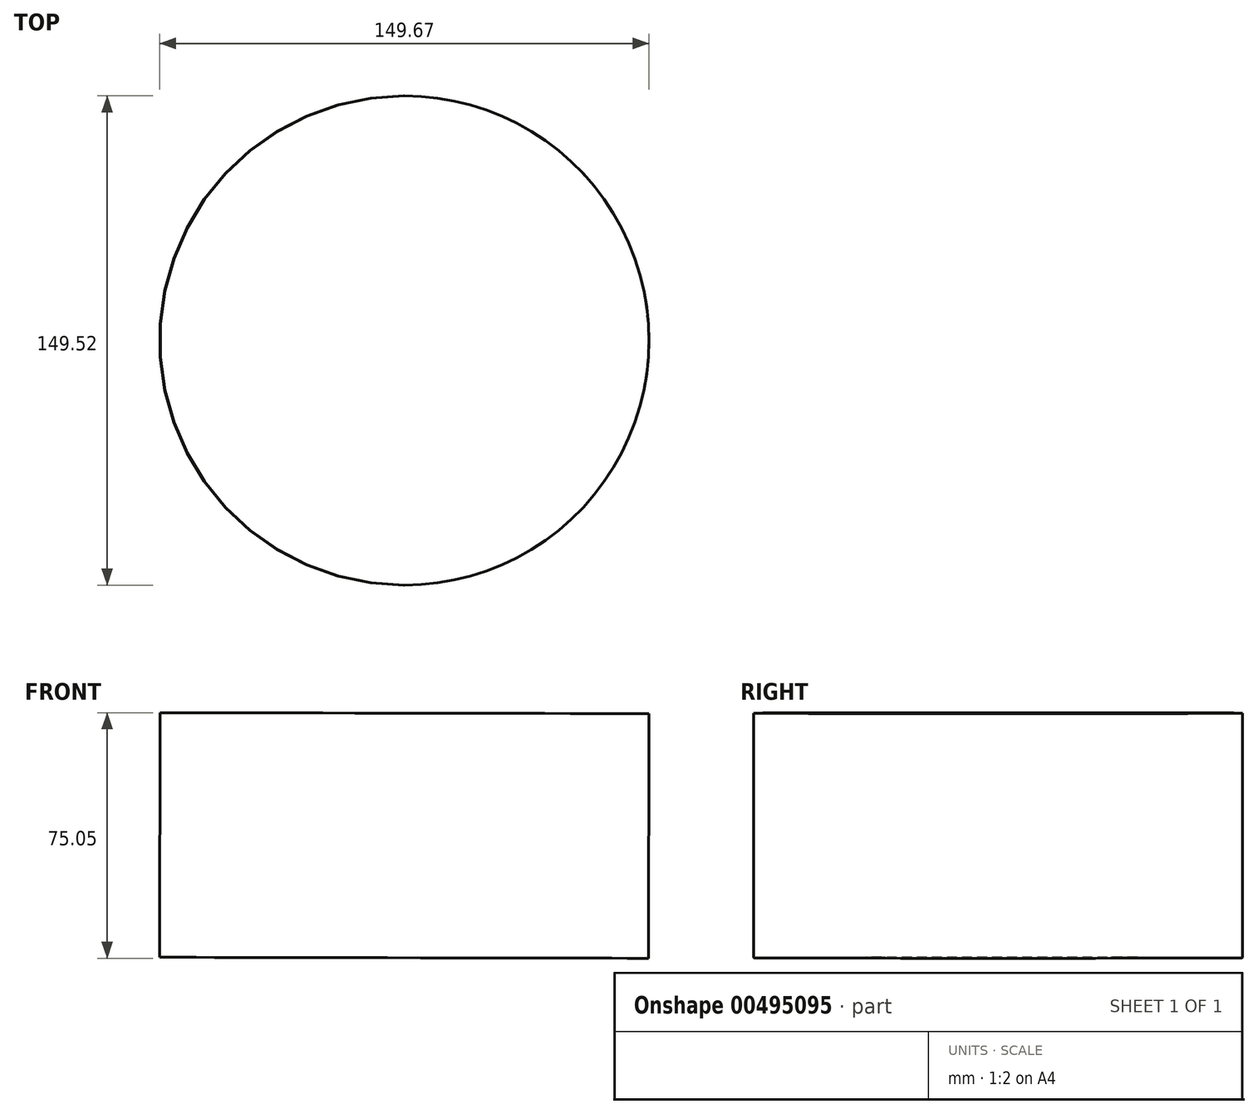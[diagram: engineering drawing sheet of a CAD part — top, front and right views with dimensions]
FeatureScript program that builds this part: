
annotation { "Feature Type Name" : "Feature", "Feature Type Description" : "" }
export const myFeature = defineFeature(function(context is Context, id is Id, definition is map)
    precondition{}
    {
        {
            var Q0;
            Q0=qCreatedBy(makeId("Front.planeOp"),FACE);
            var sketch = newSketch(context, id + "F0", { "sketchPlane" : qUnion([Q0])});
            skCircle(sketch, "E0.cCircle", {"center": v(0, 0) * mm, "radius": 52.87 * mm, "construction": true});
            skLineSegment(sketch, "E0.0", {"start": v(37.45, 37.3) * mm, "end": v(37.3, -37.45) * mm});
            skLineSegment(sketch, "E0.1", {"start": v(37.3, -37.45) * mm, "end": v(-37.45, -37.3) * mm});
            skLineSegment(sketch, "E0.2", {"start": v(-37.45, -37.3) * mm, "end": v(-37.3, 37.45) * mm});
            skLineSegment(sketch, "E0.3", {"start": v(-37.3, 37.45) * mm, "end": v(37.45, 37.3) * mm});
            skSolve(sketch);
        }
        {
            var Q0;
            Q0=makeQuery(id+"F0.imprint","IMPRINT",FACE,{"disambiguationData":[TD([[makeQuery(id+"F0.imprint","IMPRINT",EDGE,{"derivedFrom":sQuery(id+"F0.wireOp",EDGE,"E0.0")}),-1.0]])]});
            var Q1;
            Q1=sQuery(id+"F0.wireOp",EDGE,"E0.0");
            revolve(context, id + "F1", {"entities" : qUnion([Q0]), "axis" : qUnion([Q1]), "revolveType" : RevolveType.FULL});
        }
    });
